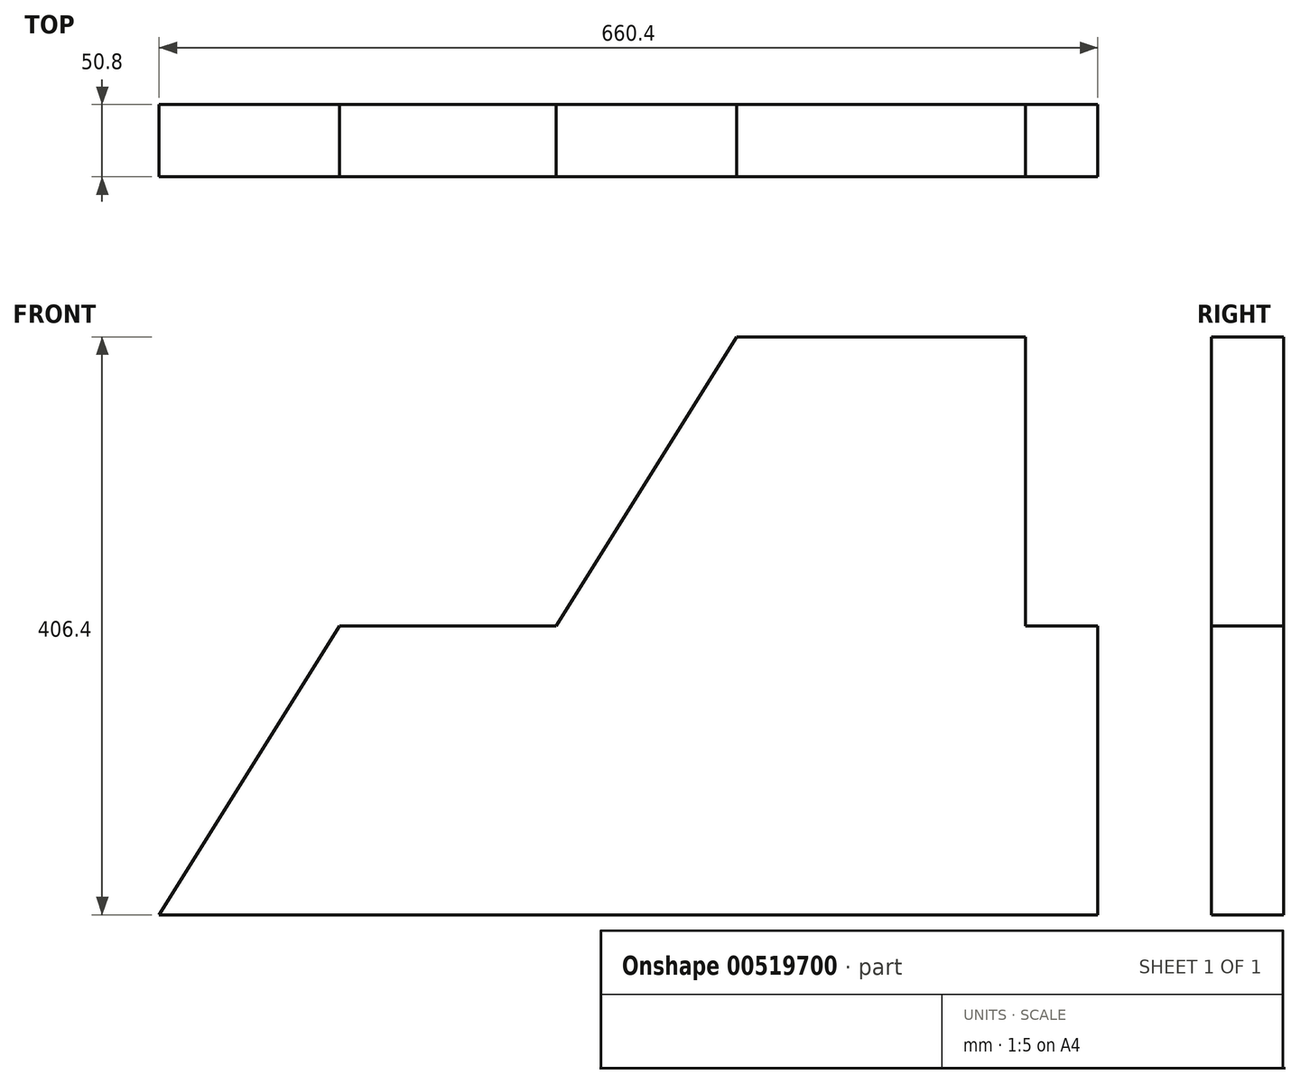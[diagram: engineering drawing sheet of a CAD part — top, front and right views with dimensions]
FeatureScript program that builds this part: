
annotation { "Feature Type Name" : "Feature", "Feature Type Description" : "" }
export const myFeature = defineFeature(function(context is Context, id is Id, definition is map)
    precondition{}
    {
        {
            var Q0;
            Q0=qCreatedBy(makeId("Front.planeOp"),FACE);
            var sketch = newSketch(context, id + "F0", { "sketchPlane" : qUnion([Q0])});
            skLineSegment(sketch, "E0", {"start": v(0, 0) * mm, "end": v(-660.4, 0) * mm});
            skLineSegment(sketch, "E1", {"start": v(0, 0) * mm, "end": v(0, 203.2) * mm});
            skLineSegment(sketch, "E2", {"start": v(0, 203.2) * mm, "end": v(-50.8, 203.2) * mm});
            skLineSegment(sketch, "E3", {"start": v(-50.8, 203.2) * mm, "end": v(-50.8, 406.4) * mm});
            skLineSegment(sketch, "E4", {"start": v(-50.8, 406.4) * mm, "end": v(-254, 406.4) * mm});
            skLineSegment(sketch, "E5", {"start": v(-381, 203.2) * mm, "end": v(-533.4, 203.2) * mm});
            skLineSegment(sketch, "E6", {"start": v(-533.4, 203.2) * mm, "end": v(-660.4, 0) * mm});
            skLineSegment(sketch, "E7", {"start": v(-254, 406.4) * mm, "end": v(-381, 203.2) * mm});
            skSolve(sketch);
        }
        {
            var Q0;
            Q0 = qSketchRegion(id + "F0", true);
            extrude(context, id + "F1", {"entities" : qUnion([Q0]), "depth" : 50.8 * mm, "offsetDistance" : 25.4 * mm});
        }
    });
